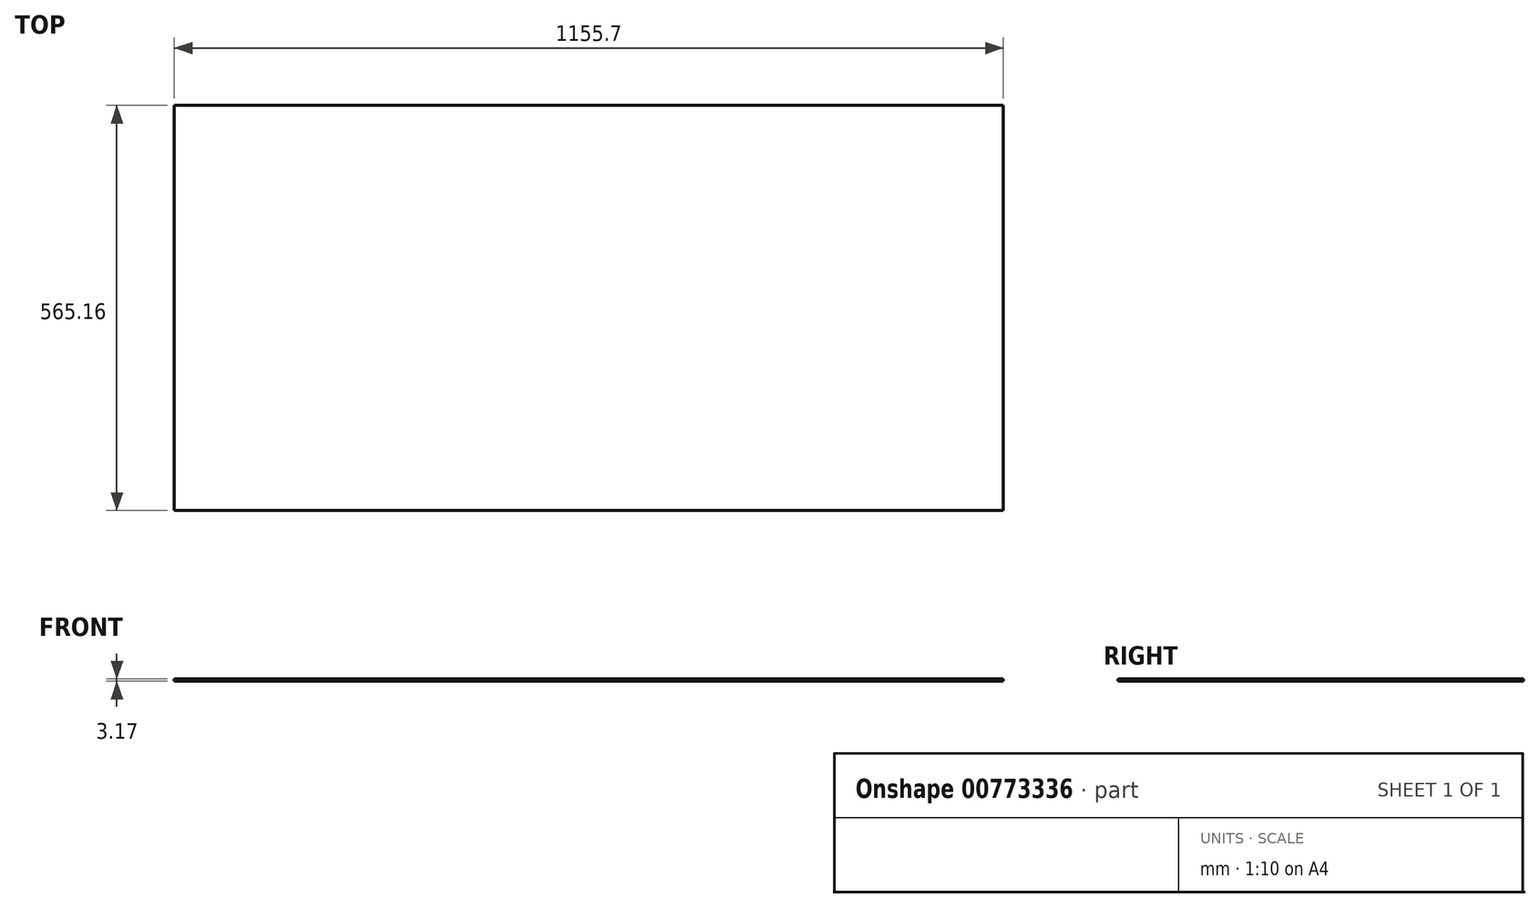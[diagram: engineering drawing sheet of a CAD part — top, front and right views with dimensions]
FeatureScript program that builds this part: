
annotation { "Feature Type Name" : "Feature", "Feature Type Description" : "" }
export const myFeature = defineFeature(function(context is Context, id is Id, definition is map)
    precondition{}
    {
        {
            var Q0;
            Q0=qCreatedBy(makeId("Top.planeOp"),FACE);
            var sketch = newSketch(context, id + "F0", { "sketchPlane" : qUnion([Q0])});
            skLineSegment(sketch, "E0.bottom", {"start": v(577.85, 282.58) * mm, "end": v(-577.85, 282.58) * mm});
            skLineSegment(sketch, "E0.top", {"start": v(577.85, -282.58) * mm, "end": v(-577.85, -282.58) * mm});
            skLineSegment(sketch, "E0.left", {"start": v(577.85, 282.58) * mm, "end": v(577.85, -282.58) * mm});
            skLineSegment(sketch, "E0.right", {"start": v(-577.85, 282.58) * mm, "end": v(-577.85, -282.58) * mm});
            skPoint(sketch, "E0.middle", {"position": v(0, 0) * mm});
            skSolve(sketch);
        }
        {
            var Q0;
            Q0 = qSketchRegion(id + "F0", true);
            extrude(context, id + "F1", {"entities" : qUnion([Q0]), "depth" : 3.17 * mm, "offsetDistance" : 25.4 * mm});
        }
    });
